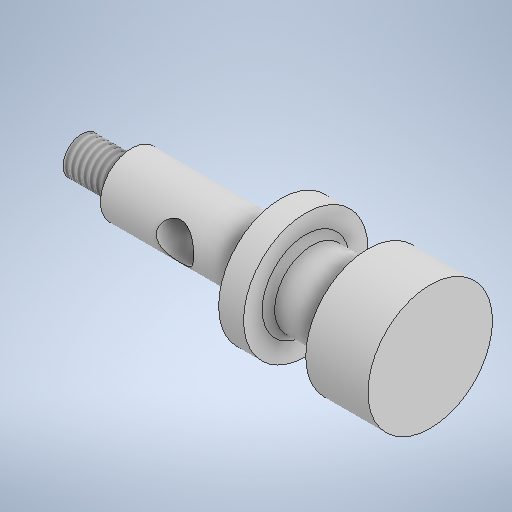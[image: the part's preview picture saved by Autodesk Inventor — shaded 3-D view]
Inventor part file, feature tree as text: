
AUTODESK INVENTOR PART (.ipt)
format: ipt  version: 2025.1 (Build 291241000, 241)  size: 314,368 bytes
history: native  units: mm
features: sketch x3, hole x2, thread x2, revolve x1, plane x1, fillet x1
ambient origin geometry x8: Origin, YZ Plane, XZ Plane, XY Plane, X Axis, Y Axis, Z Axis, Center Point
bodies: Solid1 (feature_tree)
feature tree (10):
  revolve  "Revolution1"  [1 undecoded]
  plane  "Work Plane1"
  hole  "Hole1"  [1 undecoded]
  thread  "Thread1"  [1 undecoded]
  fillet  "Fillet1"  Radius=3.0mm
  hole  "Hole2"  [1 undecoded]
  thread  "Thread2"  [1 undecoded]
  sketch  "Sketch1"  dims[d0=28.0mm d1=5.0mm]
  sketch  "Sketch2"  dims[d2=5.0mm d3=2.0mm d4=12.0mm d5=3.0mm]
  sketch  "Sketch4"  dims[d6=5.0mm d7=10.0mm d8=6.0mm d9=90.0deg d10=2.5mm d11=6.0mm d12=3.0mm d13=6.0mm d14=4.0mm d15=2.0mm d16=90.0deg d17=8.0mm d18=20.594885mm d19=10.0mm d20=0.0mm d21=0.5mm d22=2.5mm d23=3.0mm d24=6.0mm d25=4.0mm d26=2.0mm d27=90.0deg d28=8.0mm d29=20.594885mm d30=10.0mm d31=0.0mm]
note: 5 required parameter values undecoded (feature->parameter linkage not recoverable at this tier; creation-order binding heuristic only, values carry confidence <= 0.55)